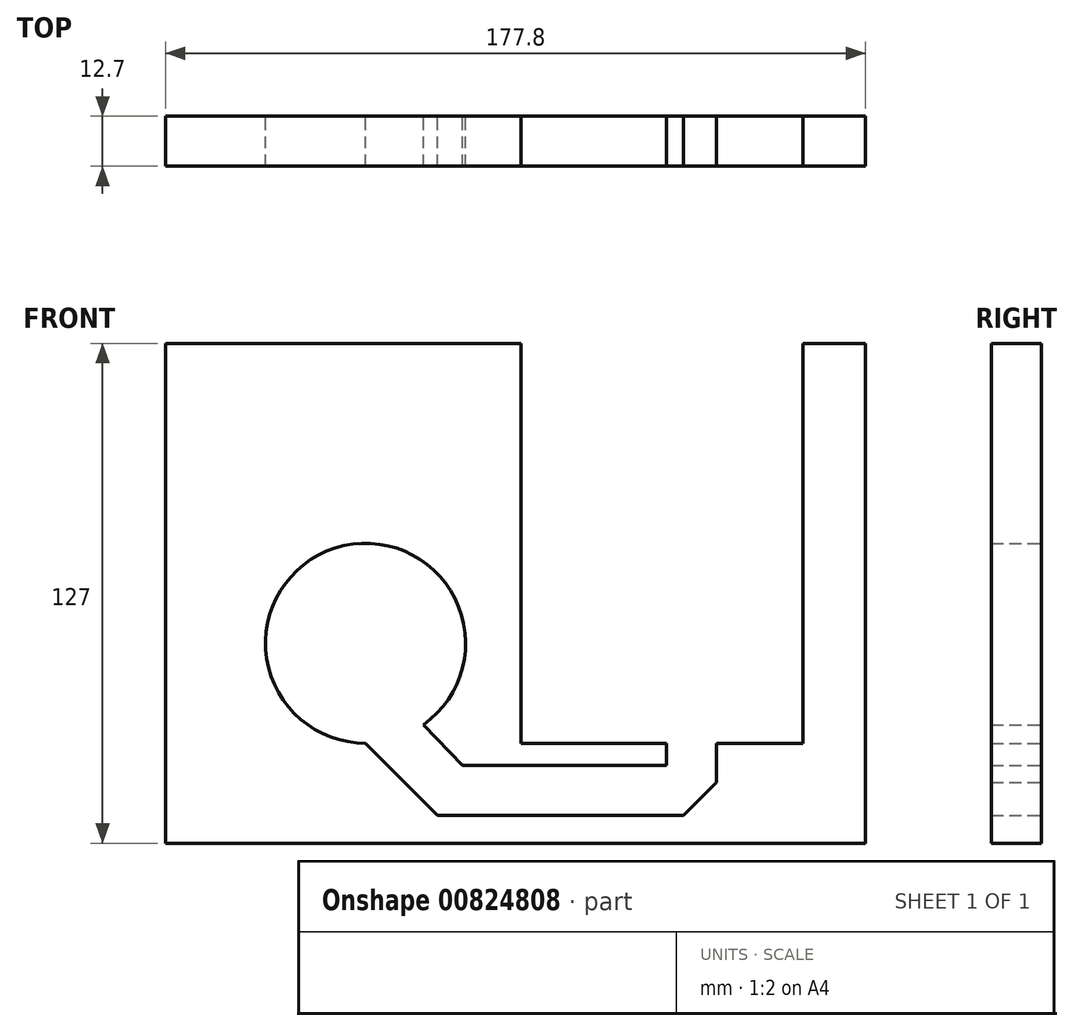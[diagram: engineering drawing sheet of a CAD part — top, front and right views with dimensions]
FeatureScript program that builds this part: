
annotation { "Feature Type Name" : "Feature", "Feature Type Description" : "" }
export const myFeature = defineFeature(function(context is Context, id is Id, definition is map)
    precondition{}
    {
        {
            var Q0;
            Q0=qCreatedBy(makeId("Front.planeOp"),FACE);
            var sketch = newSketch(context, id + "F0", { "sketchPlane" : qUnion([Q0])});
            skLineSegment(sketch, "E0", {"start": v(-97.28, 101.6) * mm, "end": v(-97.28, -25.4) * mm});
            skLineSegment(sketch, "E1", {"start": v(-97.28, -25.4) * mm, "end": v(80.52, -25.4) * mm});
            skLineSegment(sketch, "E2", {"start": v(80.52, -25.4) * mm, "end": v(80.52, 101.6) * mm});
            skLineSegment(sketch, "E3", {"start": v(-97.28, 101.6) * mm, "end": v(-6.93, 101.6) * mm});
            skLineSegment(sketch, "E4", {"start": v(-6.93, 101.6) * mm, "end": v(-6.93, 0) * mm});
            skArc(sketch, "E5", {"start": v(-31.77, 4.7) * mm, "mid": v(-54.2, 49.6) * mm, "end": v(-46.48, 0) * mm});
            skLineSegment(sketch, "E6", {"start": v(80.52, 101.6) * mm, "end": v(64.65, 101.6) * mm});
            skLineSegment(sketch, "E7", {"start": v(64.65, 101.6) * mm, "end": v(64.65, 0) * mm});
            skLineSegment(sketch, "E8", {"start": v(-6.93, 0) * mm, "end": v(29.97, 0) * mm});
            skLineSegment(sketch, "E9", {"start": v(64.65, 0) * mm, "end": v(42.67, 0) * mm});
            skLineSegment(sketch, "E10", {"start": v(42.67, 0) * mm, "end": v(42.67, -9.95) * mm});
            skLineSegment(sketch, "E11", {"start": v(42.67, -9.95) * mm, "end": v(34.3, -18.32) * mm});
            skLineSegment(sketch, "E12", {"start": v(34.3, -18.32) * mm, "end": v(-28.16, -18.32) * mm});
            skLineSegment(sketch, "E13", {"start": v(-28.16, -18.32) * mm, "end": v(-46.48, 0) * mm});
            skLineSegment(sketch, "E14", {"start": v(29.97, 0) * mm, "end": v(29.97, -5.62) * mm});
            skLineSegment(sketch, "E15", {"start": v(29.97, -5.62) * mm, "end": v(-21.8, -5.62) * mm});
            skLineSegment(sketch, "E16", {"start": v(-21.8, -5.62) * mm, "end": v(-31.77, 4.7) * mm});
            skSolve(sketch);
        }
        {
            var Q0;
            Q0 = qSketchRegion(id + "F0", true);
            extrude(context, id + "F1", {"entities" : qUnion([Q0]), "depth" : 12.7 * mm, "offsetDistance" : 25 * mm});
        }
    });
